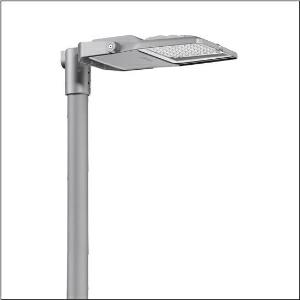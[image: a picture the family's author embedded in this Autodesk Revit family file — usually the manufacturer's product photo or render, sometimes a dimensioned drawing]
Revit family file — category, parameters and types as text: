
# Revit family: floodlight_fl_21_mini___pl43_5xa7776c2a3a_c8bd
name_source: partatom
category: Lighting Fixtures
units: mm (PartAtom-declared; Revit-internal decimal feet)

## family parameters
Cut with Voids When Loaded = No
Host = Face
Light Source = No
Part Type = Normal
Room Calculation Point = No
Round Connector Dimension = Use Diameter
Shared = No

## types (1)
- --- (1 x LED, 12500 lm, 89 W, 3000K)
    Apparent Load = 89 VA
    CIE Flux Codes = 27 78 99 100 100
    Color Rendering = 70
    Color Temperature = 3000K
    Default Elevation = 1800 mm
    Description = Floodlight FL 21 mini, floodlight, primary light control with lens, of PMMA, primary optical cover: protective disc, of toughened safety glass, transparent, light distribution: PL43, light emission: direct distribution, installation type: surface-mounted, LED, High Power LED, rated luminous flux: 12.500lm, luminous efficacy: 140lm/W, light colour: 730, colour temperature: 3000K, control: flexible luminous flux parameterisation, time-dependent luminous flux control, constant luminous flux control, overheat protection, presetting dimming logarithmic, with terminal, 6-pole, mains connection: 220..240V, AC, 50/60Hz, start of lifetime: 89W, end of service life: 94W, reduction: 43W, luminaire housing, of diecast aluminium, powder-coated, Siteco® metallic grey (DB 702S), corrosivity category C5 mid according to DIN EN ISO 12944, sealing non-destructively replaceable, please order mast flange separately, mast bracket, of steel, galvanised, powder-coated, Siteco® metallic grey (DB 702S), Smart Interface below and above, protection rating (complete): IP66, insulation class (complete): insulation class II (safety insulation), certification: CE, ENEC, VDE, protection symbol: D, impact resistance: IK08, permissible operating ambient temperature: -40..+40°C, permissible operating ambient temperature for outdoor applications: -40..+50°C, standard: DIN EN 12944, LABS conformity tested according to VDMA 24364:2018-05, packaging unit: 1 piece

Light Distribution: PL43
    Height = 70 mm
    Lamp = 1 x LED
    Lamp Light Flux = 12500 lm
    Lamp Power = 89 W
    Lamp count = 1
    Length = 485 mm
    Luminous efficacy = 140 lm/W
    Manufacturer = Siteco
    ModVariant = No
    Model = 5XA7776C2A3A
    Number of Poles = 1
    OnlyDefault = Yes
    Power Factor = 1
    Product Name = Floodlight FL 21 mini | PL43
    Product group = floodlight | pylon annexe
    ProductGroupID = 6200
    Protection Class = Protection class II
    Protection Degree = IP 66
    RLX_Detail_Level = 1
    RLX_Emergency_Light_Flux = 0 lm
    RLX_Emergency_Type = 0
    RLX_Emergency_Type_DB = No
    RlxData = <blob elided: 100829 chars, md5=70114ba8>
    Socket = socket
    Standby Power = 0 W
    System Light Flux = 12500 lm
    System Power = 89 W
    Type Comments = factory setting: luminous flux: 100 % | dim-lin: 254 | 456 mA
    Type Image = l_1007125.jpg
    URL = http://relux.com
    VarID = @adj_111247
    Voltage = 0 V
    Weight = 0.00 kg
    Width = 337 mm

## geometry (parser evidence)
native form markers: Blend x4, Sweep x14
no freeform markers — native parametric forms only
